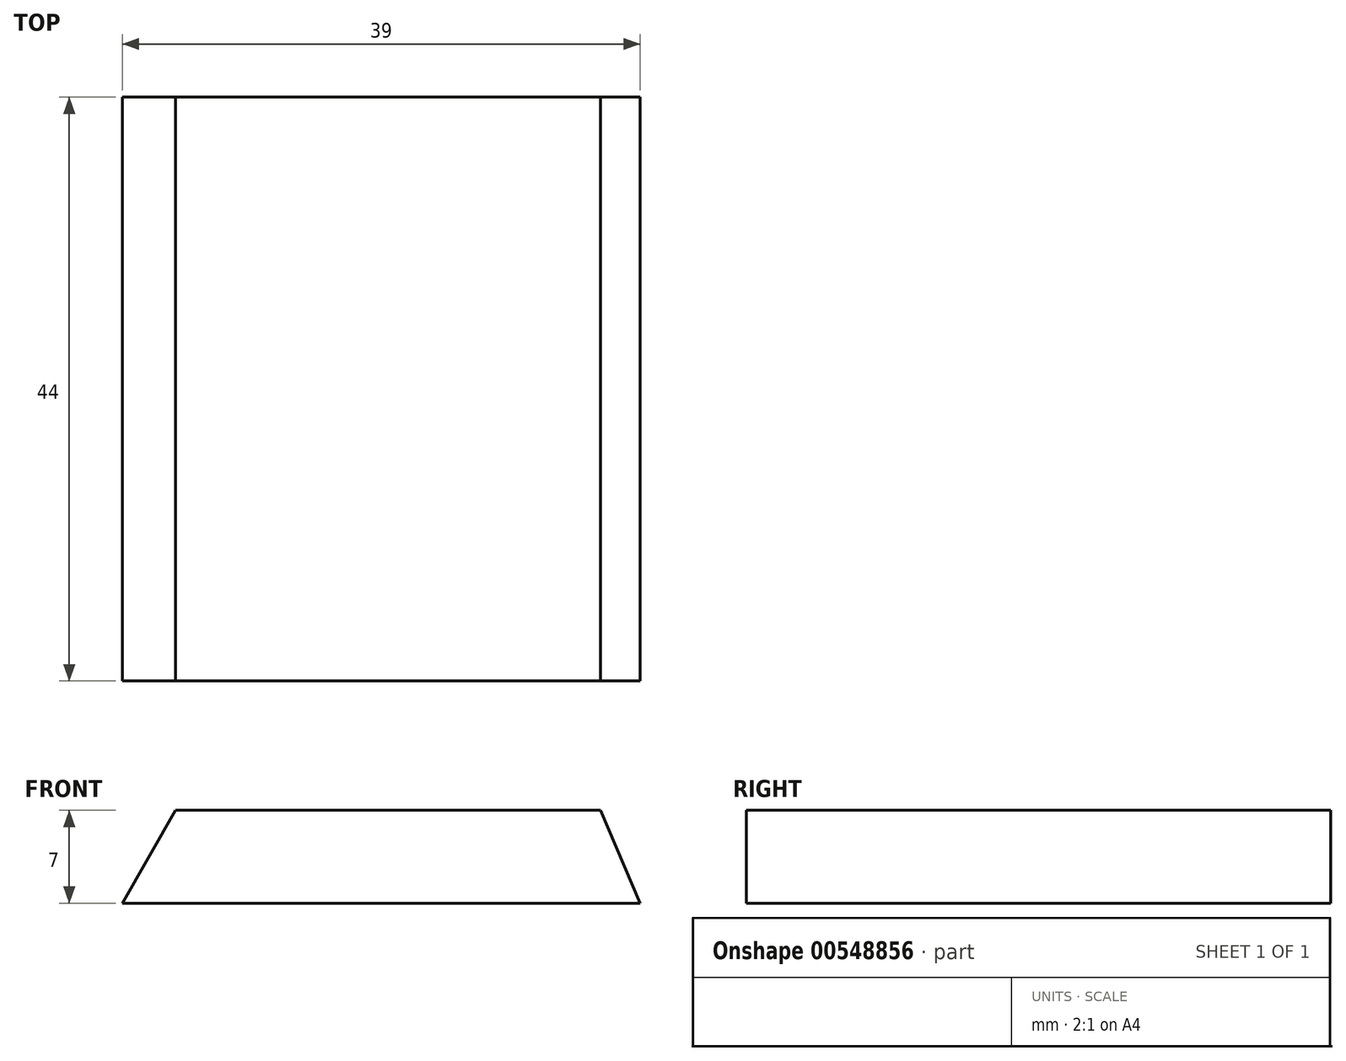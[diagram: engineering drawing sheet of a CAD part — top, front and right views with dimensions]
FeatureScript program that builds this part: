
annotation { "Feature Type Name" : "Feature", "Feature Type Description" : "" }
export const myFeature = defineFeature(function(context is Context, id is Id, definition is map)
    precondition{}
    {
        {
            var Q0;
            Q0=qCreatedBy(makeId("Top.planeOp"),FACE);
            var sketch = newSketch(context, id + "F0", { "sketchPlane" : qUnion([Q0])});
            skLineSegment(sketch, "E0.bottom", {"start": v(19.5, 22) * mm, "end": v(-19.5, 22) * mm});
            skLineSegment(sketch, "E0.top", {"start": v(19.5, -22) * mm, "end": v(-19.5, -22) * mm});
            skLineSegment(sketch, "E0.left", {"start": v(19.5, 22) * mm, "end": v(19.5, -22) * mm});
            skLineSegment(sketch, "E0.right", {"start": v(-19.5, 22) * mm, "end": v(-19.5, -22) * mm});
            skPoint(sketch, "E0.middle", {"position": v(0, 0) * mm});
            skSolve(sketch);
        }
        {
            var Q0;
            Q0=makeQuery(id+"F0.imprint","IMPRINT",FACE,{"disambiguationData":[TD([[makeQuery(id+"F0.imprint","IMPRINT",EDGE,{"derivedFrom":sQuery(id+"F0.wireOp",EDGE,"E0.bottom")}),1.0]])]});
            extrude(context, id + "F1", {"entities" : qUnion([Q0]), "depth" : 7 * mm});
        }
        {
            var Q0;
            Q0=makeQuery(id+"F1.opExtrude","SWEPT_FACE",FACE,{"disambiguationData":[OSD([sQuery(id+"F0.wireOp",EDGE,"E0.top")])]});
            var sketch = newSketch(context, id + "F2", { "sketchPlane" : qUnion([Q0])});
            skLineSegment(sketch, "E1", {"start": v(-19.5, 0) * mm, "end": v(-15.5, 7) * mm});
            skLineSegment(sketch, "E2", {"start": v(19.5, 0) * mm, "end": v(16.5, 7) * mm});
            skSolve(sketch);
        }
        {
            var Q0;
            {var subQ0=sQuery(id+"F2.wireOp",EDGE,"E1");Q0=makeQuery(id+"F2.imprint","IMPRINT",FACE,{"disambiguationData":[TD([[makeQuery(id+"F2.imprint","IMPRINT",EDGE,{"derivedFrom":subQ0}),1.0]])]});}
            var Q1;
            {var subQ0=sQuery(id+"F2.wireOp",EDGE,"E2");Q1=makeQuery(id+"F2.imprint","IMPRINT",FACE,{"disambiguationData":[TD([[makeQuery(id+"F2.imprint","IMPRINT",EDGE,{"derivedFrom":subQ0}),-1.0]])]});}
            extrude(context, id + "F3", {"entities" : qUnion([Q0, Q1]), "operationType" : NewBodyOperationType.REMOVE, "oppositeDirection" : true, "depth" : 44 * mm, "offsetDistance" : 25 * mm});
        }
    });
